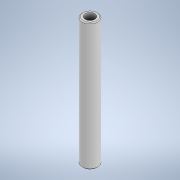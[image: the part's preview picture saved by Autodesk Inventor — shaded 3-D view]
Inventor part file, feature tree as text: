
AUTODESK INVENTOR PART (.ipt)
format: ipt  version: 2020 (Build 240168000, 168)  size: 102,912 bytes
history: native  units: mm
features: extrude x1, chamfer x1, sketch x1
ambient origin geometry x8: Origin, YZ Plane, XZ Plane, XY Plane, X Axis, Y Axis, Z Axis, Center Point
bodies: Solid1 (feature_tree)
feature tree (3):
  extrude  "Extrusion1"  Depth=65.0mm
  chamfer  "Chamfer1"  Distance=65.0mm
  sketch  "Sketch1"  dims[d0=8.0mm d1=5.0mm d2=65.0mm d3=0.0mm d4=0.5mm d5=2.0mm d6=45.0deg]
